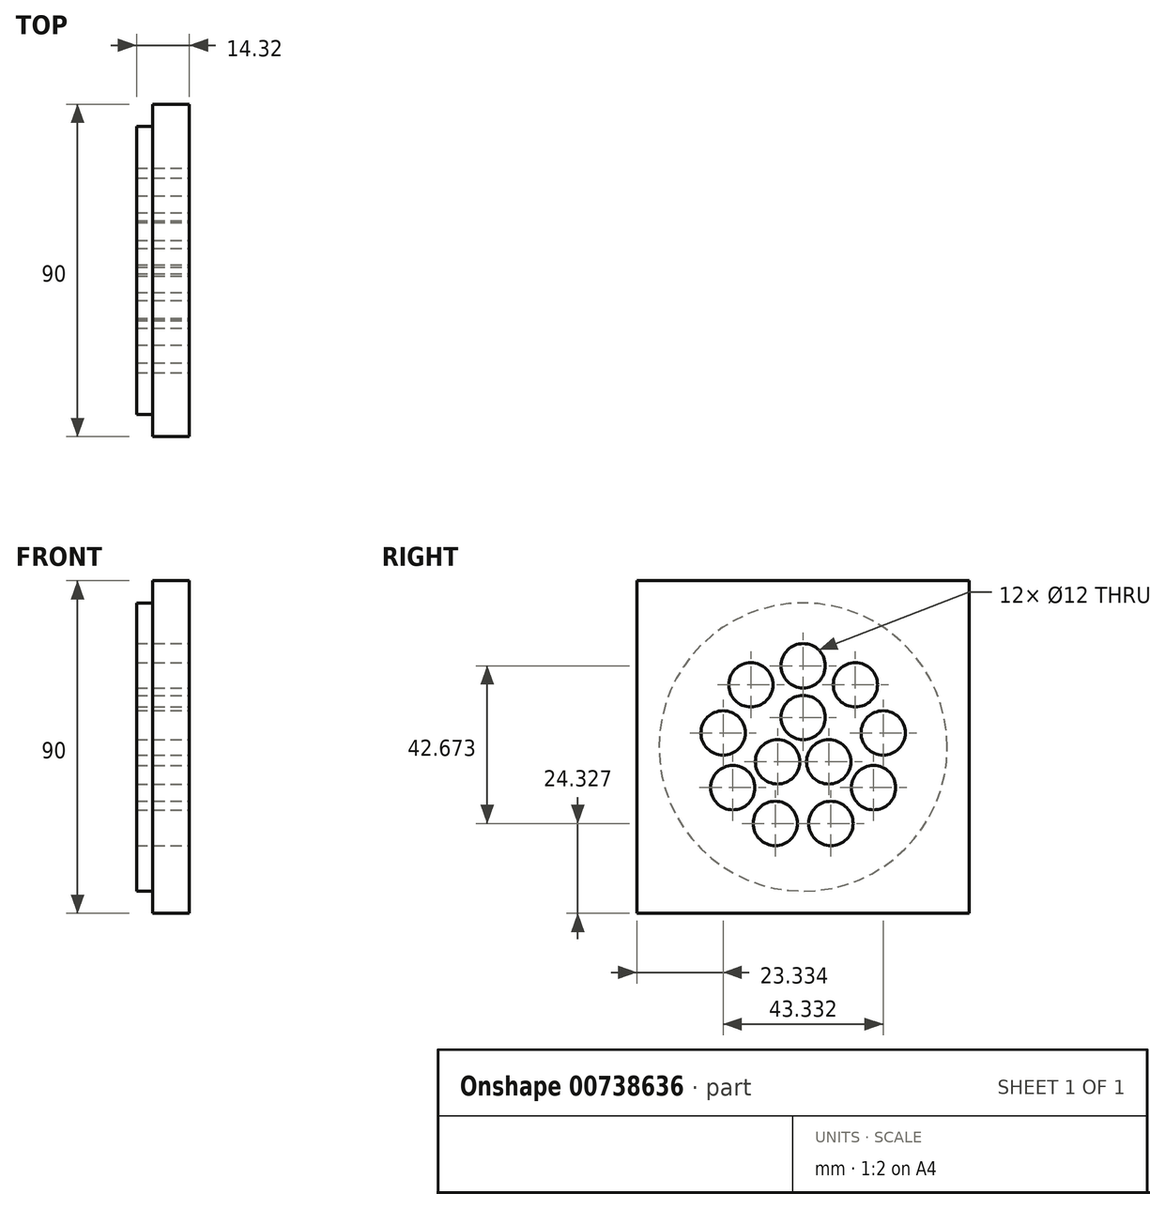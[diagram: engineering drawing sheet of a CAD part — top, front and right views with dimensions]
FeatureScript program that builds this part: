
annotation { "Feature Type Name" : "Feature", "Feature Type Description" : "" }
export const myFeature = defineFeature(function(context is Context, id is Id, definition is map)
    precondition{}
    {
        {
            var Q0;
            Q0=qCreatedBy(makeId("Front.planeOp"),FACE);
            var sketch = newSketch(context, id + "F0", { "sketchPlane" : qUnion([Q0])});
            skLineSegment(sketch, "E0", {"start": v(0, 0) * mm, "end": v(0, 32.5) * mm});
            skLineSegment(sketch, "E1", {"start": v(0, 32.5) * mm, "end": v(-10, 32.5) * mm});
            skLineSegment(sketch, "E2", {"start": v(-10, 39) * mm, "end": v(-14.32, 39) * mm});
            skLineSegment(sketch, "E3", {"start": v(0, 0) * mm, "end": v(-91.15, 0) * mm, "construction": true});
            skLineSegment(sketch, "E4", {"start": v(0, 32.5) * mm, "end": v(0, 49) * mm});
            skLineSegment(sketch, "E5", {"start": v(0, 49) * mm, "end": v(-10, 49) * mm});
            skLineSegment(sketch, "E6", {"start": v(-10, 49) * mm, "end": v(-10, 0) * mm});
            skLineSegment(sketch, "E7", {"start": v(-10, 0) * mm, "end": v(0, 0) * mm});
            skLineSegment(sketch, "E8", {"start": v(-14.32, 32.5) * mm, "end": v(-14.32, 0) * mm});
            skLineSegment(sketch, "E9", {"start": v(-14.32, 0) * mm, "end": v(-10, 0) * mm});
            skLineSegment(sketch, "E10", {"start": v(-14.32, 32.5) * mm, "end": v(-14.32, 34.46) * mm});
            skLineSegment(sketch, "E11", {"start": v(-14.32, 34.46) * mm, "end": v(-14.32, 39) * mm});
            skSolve(sketch);
        }
        {
            var Q0;
            Q0=makeQuery(id+"F0.imprint","IMPRINT",FACE,{"disambiguationData":[TD([[makeQuery(id+"F0.imprint","IMPRINT",EDGE,{"derivedFrom":sQuery(id+"F0.wireOp",EDGE,"E2")}),1.0]])]});
            var Q1;
            Q1=sQuery(id+"F0.wireOp",EDGE,"E3");
            var Q2;
            Q2=sQuery(id+"F0.wireOp",EDGE,"E3");
            revolve(context, id + "F1", {"surfaceOperationType" : NewSurfaceOperationType.NEW, "entities" : qUnion([Q0]), "surfaceEntities" : qUnion([Q1]), "axis" : qUnion([Q2]), "revolveType" : RevolveType.FULL});
        }
        {
            var Q0;
            Q0=qCreatedBy(makeId("Right.planeOp"),FACE);
            var sketch = newSketch(context, id + "F2", { "sketchPlane" : qUnion([Q0])});
            skPoint(sketch, "E12", {"position": v(0, 0) * mm});
            skPoint(sketch, "E13.0.midPoint", {"position": v(0, 8) * mm});
            skPoint(sketch, "E14", {"position": v(-6.93, -4) * mm});
            skPoint(sketch, "E15", {"position": v(6.93, -4) * mm});
            skPoint(sketch, "E16", {"position": v(-14.14, 16.85) * mm});
            skPoint(sketch, "E17", {"position": v(0, 22) * mm});
            skPoint(sketch, "E18", {"position": v(14.14, 16.85) * mm});
            skPoint(sketch, "E19", {"position": v(21.67, 3.82) * mm});
            skPoint(sketch, "E20", {"position": v(19.05, -11) * mm});
            skPoint(sketch, "E21", {"position": v(7.52, -20.67) * mm});
            skPoint(sketch, "E22", {"position": v(-7.52, -20.67) * mm});
            skPoint(sketch, "E23", {"position": v(-19.05, -11) * mm});
            skPoint(sketch, "E24", {"position": v(-21.67, 3.82) * mm});
            skLineSegment(sketch, "E25.bottom", {"start": v(-45, -45) * mm, "end": v(45, -45) * mm});
            skLineSegment(sketch, "E25.top", {"start": v(-45, 45) * mm, "end": v(45, 45) * mm});
            skLineSegment(sketch, "E25.left", {"start": v(-45, -45) * mm, "end": v(-45, 45) * mm});
            skLineSegment(sketch, "E25.right", {"start": v(45, -45) * mm, "end": v(45, 45) * mm});
            skSolve(sketch);
        }
        {
            var Q0;
            Q0=makeQuery(id+"F2.imprint","IMPRINT",FACE,{"disambiguationData":[TD([[makeQuery(id+"F2.imprint","IMPRINT",EDGE,{"derivedFrom":sQuery(id+"F2.wireOp",EDGE,"213tyaNY-octn-3ph0-H93y-aJ4PdrWAXhg4.bottom")}),-1.0]])]});
            var Q1;
            Q1=makeQuery(id+"F2.imprint","IMPRINT",FACE,{"disambiguationData":[TD([[makeQuery(id+"F2.imprint","IMPRINT",EDGE,{"derivedFrom":sQuery(id+"F2.wireOp",EDGE,"E25.bottom")}),1.0]])]});
            extrude(context, id + "F3", {"entities" : qUnion([Q0, Q1]), "operationType" : NewBodyOperationType.ADD, "oppositeDirection" : true, "depth" : 10 * mm, "offsetDistance" : 25 * mm});
        }
        {
            var Q0;
            Q0=sQuery(id+"F2.wireOp",VERTEX,"E14");
            var Q1;
            Q1=sQuery(id+"F2.wireOp",VERTEX,"E15");
            var Q2;
            Q2=sQuery(id+"F2.wireOp",VERTEX,"E13.0.midPoint");
            var Q3;
            Q3=sQuery(id+"F2.wireOp",VERTEX,"823668a7-b846-4c9e-b797-4bccdd8e680a");
            var Q4;
            Q4=sQuery(id+"F2.wireOp",VERTEX,"6f8aefd1-6fde-471b-98c0-d986d01cea9a");
            var Q5;
            Q5=sQuery(id+"F2.wireOp",VERTEX,"4d11aba2-9e73-4ca9-9560-fb374364e490");
            var Q6;
            Q6=sQuery(id+"F2.wireOp",VERTEX,"ddfc1744-d240-4fb5-9e5d-c01e82d83220.0.midPoint");
            var Q7;
            Q7=sQuery(id+"F2.wireOp",VERTEX,"2d8ed9e1-cba8-4870-9aca-e2b4c0ce7e27");
            var Q8;
            Q8=sQuery(id+"F2.wireOp",VERTEX,"6ef4e534-5ad7-4e9a-a9c9-9922eab4d70c");
            var Q9;
            Q9=sQuery(id+"F2.wireOp",VERTEX,"E24");
            var Q10;
            Q10=sQuery(id+"F2.wireOp",VERTEX,"E16");
            var Q11;
            Q11=sQuery(id+"F2.wireOp",VERTEX,"E17");
            var Q12;
            Q12=sQuery(id+"F2.wireOp",VERTEX,"E18");
            var Q13;
            Q13=sQuery(id+"F2.wireOp",VERTEX,"E19");
            var Q14;
            Q14=sQuery(id+"F2.wireOp",VERTEX,"E20");
            var Q15;
            Q15=sQuery(id+"F2.wireOp",VERTEX,"E21");
            var Q16;
            Q16=sQuery(id+"F2.wireOp",VERTEX,"E22");
            var Q17;
            Q17=sQuery(id+"F2.wireOp",VERTEX,"E23");
            var Q18;
            Q18=makeQuery(id+"F1.opRevolve","SWEPT_BODY",BODY,{"disambiguationData":[OSD([sQuery(id+"F0.wireOp",EDGE,"YgWfSLq0-zH7R-wbw6-XSP4-RkyFbBys6xV8"),sQuery(id+"F0.wireOp",EDGE,"E1"),sQuery(id+"F0.wireOp",EDGE,"E2"),sQuery(id+"F0.wireOp",EDGE,"zLC7ccXj-PyRz-rVzG-ytcT-hmyTzz9YcY4z"),sQuery(id+"F0.wireOp",EDGE,"dCg9Ym94-fqrO-inzh-IeUa-A3a6M2CNHAVO"),sQuery(id+"F0.wireOp",EDGE,"E4"),sQuery(id+"F0.wireOp",EDGE,"E5"),sQuery(id+"F0.wireOp",EDGE,"E6")])]});
            hole(context, id + "F4", {"style" : HoleStyle.SIMPLE, "endStyle" : HoleEndStyle.BLIND, "holeDiameter" : 12 * mm, "majorDiameter" : 5 * mm, "holeDepth" : 20 * mm, "isTappedThrough" : true, "tappedDepth" : 8 * mm, "tapClearance" : 3, "startFromSketch" : true, "locations" : qUnion([Q0, Q1, Q2, Q3, Q4, Q5, Q6, Q7, Q8, Q9, Q10, Q11, Q12, Q13, Q14, Q15, Q16, Q17]), "scope" : qUnion([Q18])});
        }
    });
